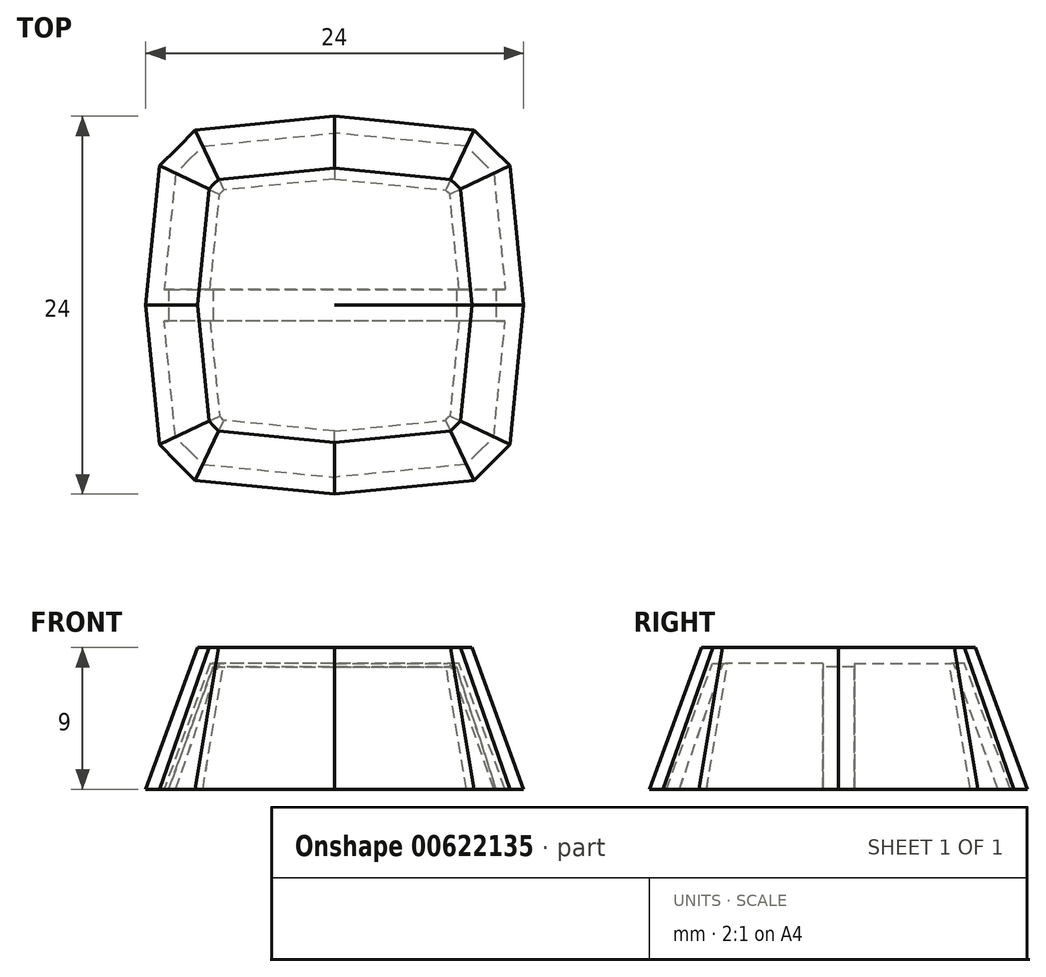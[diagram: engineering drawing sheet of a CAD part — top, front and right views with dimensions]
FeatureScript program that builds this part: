
annotation { "Feature Type Name" : "Feature", "Feature Type Description" : "" }
export const myFeature = defineFeature(function(context is Context, id is Id, definition is map)
    precondition{}
    {
        {
            var Q0;
            Q0=qCreatedBy(makeId("Top.planeOp"),FACE);
            var sketch = newSketch(context, id + "F0", { "sketchPlane" : qUnion([Q0])});
            skLineSegment(sketch, "E0", {"start": v(20.85, -11.13) * mm, "end": v(23.13, -8.85) * mm});
            skLineSegment(sketch, "E1", {"start": v(23.13, -8.85) * mm, "end": v(24, 0) * mm});
            skLineSegment(sketch, "E2", {"start": v(24, 0) * mm, "end": v(23.13, 8.85) * mm});
            skLineSegment(sketch, "E3", {"start": v(23.13, 8.85) * mm, "end": v(20.85, 11.13) * mm});
            skLineSegment(sketch, "E4", {"start": v(20.85, 11.13) * mm, "end": v(12, 12) * mm});
            skLineSegment(sketch, "E5", {"start": v(12, 12) * mm, "end": v(12, -12) * mm});
            skLineSegment(sketch, "E6", {"start": v(12, -12) * mm, "end": v(20.85, -11.13) * mm});
            skLineSegment(sketch, "E7.MirrorCS", {"start": v(12, -12) * mm, "end": v(3.15, -11.13) * mm});
            skLineSegment(sketch, "E8.MirrorCS", {"start": v(3.15, -11.13) * mm, "end": v(0.87, -8.85) * mm});
            skLineSegment(sketch, "E9.MirrorCS", {"start": v(0.87, -8.85) * mm, "end": v(0, 0) * mm});
            skLineSegment(sketch, "E10.MirrorCS", {"start": v(0, 0) * mm, "end": v(0.87, 8.85) * mm});
            skLineSegment(sketch, "E11.MirrorCS", {"start": v(0.87, 8.85) * mm, "end": v(3.15, 11.13) * mm});
            skLineSegment(sketch, "E12.MirrorCS", {"start": v(3.15, 11.13) * mm, "end": v(12, 12) * mm});
            skSolve(sketch);
        }
        {
            var Q0;
            Q0=makeQuery(id+"F0.imprint","IMPRINT",FACE,{"disambiguationData":[TD([[makeQuery(id+"F0.imprint","IMPRINT",EDGE,{"derivedFrom":sQuery(id+"F0.wireOp",EDGE,"E5")}),-1.0]])]});
            var Q1;
            Q1=makeQuery(id+"F0.imprint","IMPRINT",FACE,{"disambiguationData":[TD([[makeQuery(id+"F0.imprint","IMPRINT",EDGE,{"derivedFrom":sQuery(id+"F0.wireOp",EDGE,"E0")}),1.0]])]});
            extrude(context, id + "F1", {"entities" : qUnion([Q0, Q1]), "depth" : 9 * mm, "offsetDistance" : 25.4 * mm});
        }
        {
            var Q0;
            Q0=makeQuery(id+"F1.opExtrude","CAP_EDGE",EDGE,{"disambiguationData":[OSD([sQuery(id+"F0.wireOp",EDGE,"E12.MirrorCS")])],"isStart":true});
            cPlane(context, id + "F2", {"entities" : qUnion([Q0]), "cplaneType" : CPlaneType.LINE_ANGLE, "offset" : 25.4 * mm, "angle" : 20 * degree, "width" : 152.4 * mm, "height" : 152.4 * mm});
        }
        {
            var Q0;
            Q0=qCreatedBy(id+"F2.planeOp",FACE);
            var sketch = newSketch(context, id + "F3", { "sketchPlane" : qUnion([Q0])});
            skLineSegment(sketch, "E13.bottom", {"start": v(-13.55, 6.67) * mm, "end": v(4.42, 6.67) * mm});
            skLineSegment(sketch, "E13.top", {"start": v(-13.55, -6.68) * mm, "end": v(4.42, -6.68) * mm});
            skLineSegment(sketch, "E13.left", {"start": v(-13.55, 6.67) * mm, "end": v(-13.55, -6.68) * mm});
            skLineSegment(sketch, "E13.right", {"start": v(4.42, 6.67) * mm, "end": v(4.42, -6.68) * mm});
            skSolve(sketch);
        }
        {
            var Q0;
            Q0=makeQuery(id+"F3.imprint","IMPRINT",FACE,{"disambiguationData":[TD([[makeQuery(id+"F3.imprint","IMPRINT",EDGE,{"derivedFrom":sQuery(id+"F3.wireOp",EDGE,"E13.bottom")}),-1.0]])]});
            extrude(context, id + "F4", {"entities" : qUnion([Q0]), "operationType" : NewBodyOperationType.REMOVE, "depth" : 25.4 * mm, "offsetDistance" : 25.4 * mm});
        }
        {
            var Q0;
            Q0=makeQuery(id+"F1.opExtrude","CAP_EDGE",EDGE,{"disambiguationData":[OSD([sQuery(id+"F0.wireOp",EDGE,"E4")])],"isStart":true});
            cPlane(context, id + "F5", {"entities" : qUnion([Q0]), "cplaneType" : CPlaneType.LINE_ANGLE, "offset" : 25.4 * mm, "angle" : 20 * degree, "oppositeDirection" : true, "width" : 152.4 * mm, "height" : 152.4 * mm});
        }
        {
            var Q0;
            Q0=qCreatedBy(id+"F5.planeOp",FACE);
            var sketch = newSketch(context, id + "F6", { "sketchPlane" : qUnion([Q0])});
            skLineSegment(sketch, "E14.bottom", {"start": v(10.85, -6.72) * mm, "end": v(26.17, -6.72) * mm});
            skLineSegment(sketch, "E14.top", {"start": v(10.85, 9.02) * mm, "end": v(26.17, 9.02) * mm});
            skLineSegment(sketch, "E14.left", {"start": v(10.85, -6.72) * mm, "end": v(10.85, 9.02) * mm});
            skLineSegment(sketch, "E14.right", {"start": v(26.17, -6.72) * mm, "end": v(26.17, 9.02) * mm});
            skSolve(sketch);
        }
        {
            var Q0;
            Q0=makeQuery(id+"F6.imprint","IMPRINT",FACE,{"disambiguationData":[TD([[makeQuery(id+"F6.imprint","IMPRINT",EDGE,{"derivedFrom":sQuery(id+"F6.wireOp",EDGE,"E14.bottom")}),1.0]])]});
            extrude(context, id + "F7", {"entities" : qUnion([Q0]), "operationType" : NewBodyOperationType.REMOVE, "oppositeDirection" : true, "depth" : 25.4 * mm, "offsetDistance" : 25.4 * mm});
        }
        {
            var Q0;
            Q0=makeQuery(id+"F1.opExtrude","CAP_EDGE",EDGE,{"disambiguationData":[OSD([sQuery(id+"F0.wireOp",EDGE,"E11.MirrorCS")])],"isStart":true});
            cPlane(context, id + "F8", {"entities" : qUnion([Q0]), "cplaneType" : CPlaneType.LINE_ANGLE, "offset" : 25.4 * mm, "angle" : 70 * degree, "oppositeDirection" : true, "width" : 152.4 * mm, "height" : 152.4 * mm});
        }
        {
            var Q0;
            Q0=qCreatedBy(id+"F8.planeOp",FACE);
            var sketch = newSketch(context, id + "F9", { "sketchPlane" : qUnion([Q0])});
            skLineSegment(sketch, "E15.bottom", {"start": v(4.2, -15.35) * mm, "end": v(-19.19, -15.35) * mm});
            skLineSegment(sketch, "E15.top", {"start": v(4.2, 18.93) * mm, "end": v(-19.19, 18.93) * mm});
            skLineSegment(sketch, "E15.left", {"start": v(4.2, -15.35) * mm, "end": v(4.2, 18.93) * mm});
            skLineSegment(sketch, "E15.right", {"start": v(-19.19, -15.35) * mm, "end": v(-19.19, 18.93) * mm});
            skSolve(sketch);
        }
        {
            var Q0;
            Q0=makeQuery(id+"F9.imprint","IMPRINT",FACE,{"disambiguationData":[TD([[makeQuery(id+"F9.imprint","IMPRINT",EDGE,{"derivedFrom":sQuery(id+"F9.wireOp",EDGE,"E15.bottom")}),-1.0]])]});
            extrude(context, id + "F10", {"entities" : qUnion([Q0]), "operationType" : NewBodyOperationType.REMOVE, "depth" : 25.4 * mm, "offsetDistance" : 25.4 * mm});
        }
        {
            var Q0;
            Q0=makeQuery(id+"F1.opExtrude","CAP_FACE",FACE,{"disambiguationData":[OSD([sQuery(id+"F0.wireOp",EDGE,"E0"),sQuery(id+"F0.wireOp",EDGE,"E1"),sQuery(id+"F0.wireOp",EDGE,"E2"),sQuery(id+"F0.wireOp",EDGE,"E3"),sQuery(id+"F0.wireOp",EDGE,"E4"),sQuery(id+"F0.wireOp",EDGE,"E6"),sQuery(id+"F0.wireOp",EDGE,"E7.MirrorCS"),sQuery(id+"F0.wireOp",EDGE,"E8.MirrorCS"),sQuery(id+"F0.wireOp",EDGE,"E9.MirrorCS"),sQuery(id+"F0.wireOp",EDGE,"E10.MirrorCS"),sQuery(id+"F0.wireOp",EDGE,"E11.MirrorCS"),sQuery(id+"F0.wireOp",EDGE,"E12.MirrorCS")])],"isStart":true});
            var sketch = newSketch(context, id + "F11", { "sketchPlane" : qUnion([Q0])});
            skLineSegment(sketch, "E16", {"start": v(12, 12) * mm, "end": v(12, -12) * mm});
            skLineSegment(sketch, "E17", {"start": v(12, -12) * mm, "end": v(28.1, -10.99) * mm});
            skLineSegment(sketch, "E18", {"start": v(28.1, -10.99) * mm, "end": v(25, 12.46) * mm});
            skLineSegment(sketch, "E19", {"start": v(25, 12.46) * mm, "end": v(12, 12) * mm});
            skSolve(sketch);
        }
        {
            var Q0;
            Q0=makeQuery(id+"F11.imprint","IMPRINT",FACE,{"disambiguationData":[TD([[makeQuery(id+"F11.imprint","IMPRINT",EDGE,{"derivedFrom":sQuery(id+"F11.wireOp",EDGE,"E17")}),1.0]])]});
            var Q1;
            Q1=makeQuery(id+"F11.imprint","IMPRINT",FACE,{"disambiguationData":[TD([[makeQuery(id+"F11.imprint","IMPRINT",EDGE,{"derivedFrom":sQuery(id+"F11.wireOp",EDGE,"E16")}),1.0]])]});
            extrude(context, id + "F12", {"entities" : qUnion([Q0, Q1]), "operationType" : NewBodyOperationType.REMOVE, "oppositeDirection" : true, "depth" : 25.4 * mm, "offsetDistance" : 25.4 * mm});
        }
        {
            var Q0;
            Q0=makeQuery(id+"F1.opExtrude","CAP_FACE",FACE,{"disambiguationData":[OSD([sQuery(id+"F0.wireOp",EDGE,"E0"),sQuery(id+"F0.wireOp",EDGE,"E1"),sQuery(id+"F0.wireOp",EDGE,"E2"),sQuery(id+"F0.wireOp",EDGE,"E3"),sQuery(id+"F0.wireOp",EDGE,"E4"),sQuery(id+"F0.wireOp",EDGE,"E6"),sQuery(id+"F0.wireOp",EDGE,"E7.MirrorCS"),sQuery(id+"F0.wireOp",EDGE,"E8.MirrorCS"),sQuery(id+"F0.wireOp",EDGE,"E9.MirrorCS"),sQuery(id+"F0.wireOp",EDGE,"E10.MirrorCS"),sQuery(id+"F0.wireOp",EDGE,"E11.MirrorCS"),sQuery(id+"F0.wireOp",EDGE,"E12.MirrorCS")])],"isStart":true});
            var sketch = newSketch(context, id + "F13", { "sketchPlane" : qUnion([Q0])});
            skLineSegment(sketch, "E20", {"start": v(0, 0) * mm, "end": v(12, 0) * mm});
            skLineSegment(sketch, "E21", {"start": v(12, 0) * mm, "end": v(12.37, 13.06) * mm});
            skLineSegment(sketch, "E22", {"start": v(12.37, 13.06) * mm, "end": v(-2.16, 13.06) * mm});
            skLineSegment(sketch, "E23", {"start": v(-2.16, 13.06) * mm, "end": v(0, 0) * mm});
            skSolve(sketch);
        }
        {
            var Q0;
            {var subQ1=sQuery(id+"F13.wireOp",EDGE,"E21");Q0=makeQuery(id+"F13.imprint","IMPRINT",FACE,{"disambiguationData":[TD([[makeQuery(id+"F13.imprint","IMPRINT",EDGE,{"derivedFrom":subQ1}),1.0]])]});}
            var Q1;
            {var subQ1=sQuery(id+"F13.wireOp",EDGE,"E20");Q1=makeQuery(id+"F13.imprint","IMPRINT",FACE,{"disambiguationData":[TD([[makeQuery(id+"F13.imprint","IMPRINT",EDGE,{"derivedFrom":subQ1}),1.0]])]});}
            extrude(context, id + "F14", {"entities" : qUnion([Q0, Q1]), "operationType" : NewBodyOperationType.REMOVE, "oppositeDirection" : true, "depth" : 25.4 * mm, "offsetDistance" : 25.4 * mm});
        }
        {
            var Q0;
            Q0=makeQuery(id+"F1.opExtrude","CAP_FACE",FACE,{"disambiguationData":[OSD([sQuery(id+"F0.wireOp",EDGE,"E0"),sQuery(id+"F0.wireOp",EDGE,"E1"),sQuery(id+"F0.wireOp",EDGE,"E2"),sQuery(id+"F0.wireOp",EDGE,"E3"),sQuery(id+"F0.wireOp",EDGE,"E4"),sQuery(id+"F0.wireOp",EDGE,"E6"),sQuery(id+"F0.wireOp",EDGE,"E7.MirrorCS"),sQuery(id+"F0.wireOp",EDGE,"E8.MirrorCS"),sQuery(id+"F0.wireOp",EDGE,"E9.MirrorCS"),sQuery(id+"F0.wireOp",EDGE,"E10.MirrorCS"),sQuery(id+"F0.wireOp",EDGE,"E11.MirrorCS"),sQuery(id+"F0.wireOp",EDGE,"E12.MirrorCS")])],"isStart":true});
            var sketch = newSketch(context, id + "F15", { "sketchPlane" : qUnion([Q0])});
            skLineSegment(sketch, "E24", {"start": v(2, -10) * mm, "end": v(12, 0) * mm});
            skLineSegment(sketch, "E25", {"start": v(12, 0) * mm, "end": v(-1.63, 1.68) * mm});
            skLineSegment(sketch, "E26", {"start": v(-1.63, 1.68) * mm, "end": v(-1.63, -9.8) * mm});
            skLineSegment(sketch, "E27", {"start": v(-1.63, -9.8) * mm, "end": v(2, -10) * mm});
            skSolve(sketch);
        }
        {
            var Q0;
            Q0=makeQuery(id+"F15.imprint","IMPRINT",FACE,{"disambiguationData":[TD([[makeQuery(id+"F15.imprint","IMPRINT",EDGE,{"derivedFrom":sQuery(id+"F15.wireOp",EDGE,"E25")}),1.0]])]});
            var Q1;
            {var subQ0=sQuery(id+"F15.wireOp",EDGE,"E24");Q1=makeQuery(id+"F15.imprint","IMPRINT",FACE,{"disambiguationData":[TD([[makeQuery(id+"F15.imprint","IMPRINT",EDGE,{"derivedFrom":subQ0}),1.0]])]});}
            extrude(context, id + "F16", {"entities" : qUnion([Q0, Q1]), "operationType" : NewBodyOperationType.REMOVE, "oppositeDirection" : true, "depth" : 25.4 * mm, "offsetDistance" : 25.4 * mm});
        }
        {
            var Q0;
            Q0=makeQuery(id+"F1.opExtrude","SWEPT_BODY",BODY,{"disambiguationData":[OSD([sQuery(id+"F0.wireOp",EDGE,"E0"),sQuery(id+"F0.wireOp",EDGE,"E1"),sQuery(id+"F0.wireOp",EDGE,"E2"),sQuery(id+"F0.wireOp",EDGE,"E3"),sQuery(id+"F0.wireOp",EDGE,"E4"),sQuery(id+"F0.wireOp",EDGE,"E6"),sQuery(id+"F0.wireOp",EDGE,"E7.MirrorCS"),sQuery(id+"F0.wireOp",EDGE,"E8.MirrorCS"),sQuery(id+"F0.wireOp",EDGE,"E9.MirrorCS"),sQuery(id+"F0.wireOp",EDGE,"E10.MirrorCS"),sQuery(id+"F0.wireOp",EDGE,"E11.MirrorCS"),sQuery(id+"F0.wireOp",EDGE,"E12.MirrorCS")])]});
            var Q1;
            Q1=makeQuery(id+"F16.boolean.opBoolean","COPY",FACE,{"derivedFrom":makeQuery(id+"F16.opExtrude","SWEPT_FACE",FACE,{"disambiguationData":[OSD([sQuery(id+"F15.wireOp",EDGE,"E24")])]})});
            mirror(context, id + "F17", {"operationType" : NewBodyOperationType.ADD, "entities" : qUnion([Q0]), "mirrorPlane" : qUnion([Q1])});
        }
        {
            var Q0;
            Q0=makeQuery(id+"F1.opExtrude","SWEPT_BODY",BODY,{"disambiguationData":[OSD([sQuery(id+"F0.wireOp",EDGE,"E0"),sQuery(id+"F0.wireOp",EDGE,"E1"),sQuery(id+"F0.wireOp",EDGE,"E2"),sQuery(id+"F0.wireOp",EDGE,"E3"),sQuery(id+"F0.wireOp",EDGE,"E4"),sQuery(id+"F0.wireOp",EDGE,"E6"),sQuery(id+"F0.wireOp",EDGE,"E7.MirrorCS"),sQuery(id+"F0.wireOp",EDGE,"E8.MirrorCS"),sQuery(id+"F0.wireOp",EDGE,"E9.MirrorCS"),sQuery(id+"F0.wireOp",EDGE,"E10.MirrorCS"),sQuery(id+"F0.wireOp",EDGE,"E11.MirrorCS"),sQuery(id+"F0.wireOp",EDGE,"E12.MirrorCS")])]});
            var Q1;
            Q1=makeQuery(id+"F12.boolean.opBoolean","COPY",FACE,{"derivedFrom":makeQuery(id+"F12.opExtrude","SWEPT_FACE",FACE,{"disambiguationData":[OSD([sQuery(id+"F11.wireOp",EDGE,"E16")])]})});
            mirror(context, id + "F18", {"operationType" : NewBodyOperationType.ADD, "entities" : qUnion([Q0]), "mirrorPlane" : qUnion([Q1])});
        }
        {
            var Q0;
            Q0=makeQuery(id+"F1.opExtrude","SWEPT_BODY",BODY,{"disambiguationData":[OSD([sQuery(id+"F0.wireOp",EDGE,"E0"),sQuery(id+"F0.wireOp",EDGE,"E1"),sQuery(id+"F0.wireOp",EDGE,"E2"),sQuery(id+"F0.wireOp",EDGE,"E3"),sQuery(id+"F0.wireOp",EDGE,"E4"),sQuery(id+"F0.wireOp",EDGE,"E6"),sQuery(id+"F0.wireOp",EDGE,"E7.MirrorCS"),sQuery(id+"F0.wireOp",EDGE,"E8.MirrorCS"),sQuery(id+"F0.wireOp",EDGE,"E9.MirrorCS"),sQuery(id+"F0.wireOp",EDGE,"E10.MirrorCS"),sQuery(id+"F0.wireOp",EDGE,"E11.MirrorCS"),sQuery(id+"F0.wireOp",EDGE,"E12.MirrorCS")])]});
            var Q1;
            Q1=makeQuery(id+"F17.opPattern","COPY",FACE,{"derivedFrom":makeQuery(id+"F12.boolean.opBoolean","COPY",FACE,{"derivedFrom":makeQuery(id+"F12.opExtrude","SWEPT_FACE",FACE,{"disambiguationData":[OSD([sQuery(id+"F11.wireOp",EDGE,"E16")])]})}),"instanceName":"1"});
            mirror(context, id + "F19", {"operationType" : NewBodyOperationType.ADD, "entities" : qUnion([Q0]), "mirrorPlane" : qUnion([Q1])});
        }
        {
            var Q0;
            {var subQ0=makeQuery(id+"F1.opExtrude","CAP_FACE",FACE,{"disambiguationData":[OSD([sQuery(id+"F0.wireOp",EDGE,"E0"),sQuery(id+"F0.wireOp",EDGE,"E1"),sQuery(id+"F0.wireOp",EDGE,"E2"),sQuery(id+"F0.wireOp",EDGE,"E3"),sQuery(id+"F0.wireOp",EDGE,"E4"),sQuery(id+"F0.wireOp",EDGE,"E6"),sQuery(id+"F0.wireOp",EDGE,"E7.MirrorCS"),sQuery(id+"F0.wireOp",EDGE,"E8.MirrorCS"),sQuery(id+"F0.wireOp",EDGE,"E9.MirrorCS"),sQuery(id+"F0.wireOp",EDGE,"E10.MirrorCS"),sQuery(id+"F0.wireOp",EDGE,"E11.MirrorCS"),sQuery(id+"F0.wireOp",EDGE,"E12.MirrorCS")])],"isStart":true});var subQ1=makeQuery(id+"F17.boolean.opBoolean","MERGE",FACE,{"derivedFrom":[subQ0,makeQuery(id+"F17.opPattern","COPY",FACE,{"derivedFrom":subQ0,"instanceName":"1"})]});var subQ2=makeQuery(id+"F18.boolean.opBoolean","MERGE",FACE,{"derivedFrom":[subQ1,makeQuery(id+"F18.opPattern","COPY",FACE,{"derivedFrom":subQ1,"instanceName":"1"})]});Q0=makeQuery(id+"F19.boolean.opBoolean","MERGE",FACE,{"derivedFrom":[subQ2,makeQuery(id+"F19.opPattern","COPY",FACE,{"derivedFrom":subQ2,"instanceName":"1"})]});}
            shell(context, id + "F20", {"entities" : qUnion([Q0]), "thickness" : 1 * mm});
        }
        {
            var Q0;
            {var subQ0=sQuery(id+"F11.wireOp",EDGE,"E16");Q0=makeQuery(id+"F20.opShell","OFFSET_FACE",FACE,{"disambiguationData":[OSD([subQ0]),TDD([makeQuery(id+"F19.opPattern","COPY",FACE,{"derivedFrom":makeQuery(id+"F18.opPattern","COPY",FACE,{"derivedFrom":makeQuery(id+"F17.opPattern","COPY",FACE,{"derivedFrom":makeQuery(id+"F12.boolean.opBoolean","COPY",FACE,{"derivedFrom":makeQuery(id+"F12.opExtrude","SWEPT_FACE",FACE,{"disambiguationData":[OSD([subQ0])]})}),"instanceName":"1"}),"instanceName":"1"}),"instanceName":"1"})])]});}
            var sketch = newSketch(context, id + "F21", { "sketchPlane" : qUnion([Q0])});
            skLineSegment(sketch, "E28", {"start": v(4.29, 7.78) * mm, "end": v(1.3, -0.39) * mm});
            skLineSegment(sketch, "E29", {"start": v(1.3, -0.39) * mm, "end": v(22.39, -0.39) * mm});
            skLineSegment(sketch, "E30", {"start": v(22.39, -0.39) * mm, "end": v(19.73, 7.77) * mm});
            skLineSegment(sketch, "E31", {"start": v(19.73, 7.77) * mm, "end": v(4.29, 7.78) * mm});
            skSolve(sketch);
        }
        {
            var Q0;
            {var subQ0=sQuery(id+"F21.wireOp",EDGE,"E31");Q0=makeQuery(id+"F21.imprint","IMPRINT",FACE,{"disambiguationData":[TD([[makeQuery(id+"F21.imprint","IMPRINT",EDGE,{"derivedFrom":subQ0}),1.0]])]});}
            extrude(context, id + "F22", {"entities" : qUnion([Q0]), "operationType" : NewBodyOperationType.REMOVE, "oppositeDirection" : true, "depth" : 4 * mm, "offsetDistance" : 25.4 * mm});
        }
    });
